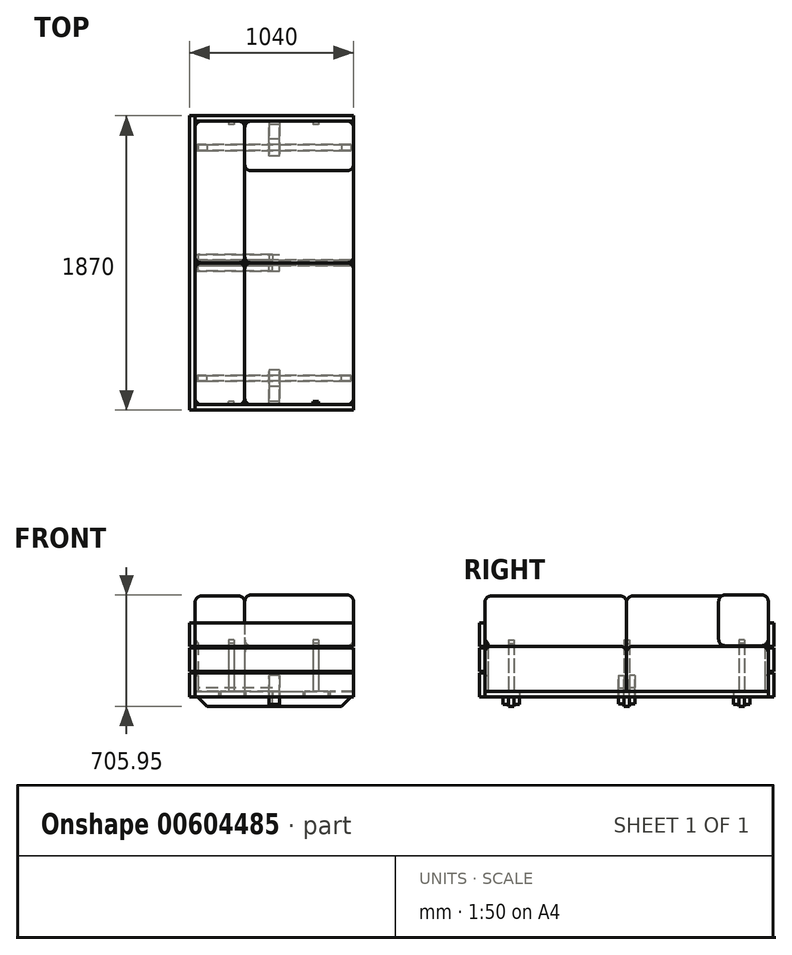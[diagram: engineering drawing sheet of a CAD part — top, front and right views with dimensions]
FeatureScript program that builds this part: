
annotation { "Feature Type Name" : "Feature", "Feature Type Description" : "" }
export const myFeature = defineFeature(function(context is Context, id is Id, definition is map)
    precondition{}
    {
        {
            var Q0;
            Q0=qCreatedBy(makeId("Front.planeOp"),FACE);
            var sketch = newSketch(context, id + "F0", { "sketchPlane" : qUnion([Q0])});
            skLineSegment(sketch, "E0.bottom", {"start": v(35, 530) * mm, "end": v(1040, 530) * mm});
            skLineSegment(sketch, "E0.top", {"start": v(35, 380) * mm, "end": v(1040, 380) * mm});
            skLineSegment(sketch, "E0.right", {"start": v(1040, 530) * mm, "end": v(1040, 380) * mm});
            skLineSegment(sketch, "E1.bottom", {"start": v(35, 370) * mm, "end": v(1040, 370) * mm});
            skLineSegment(sketch, "E1.top", {"start": v(35, 220) * mm, "end": v(1040, 220) * mm});
            skLineSegment(sketch, "E1.left", {"start": v(35, 370) * mm, "end": v(35, 220) * mm});
            skLineSegment(sketch, "E1.right", {"start": v(1040, 370) * mm, "end": v(1040, 220) * mm});
            skLineSegment(sketch, "E2.bottom", {"start": v(35, 210) * mm, "end": v(1040, 210) * mm});
            skLineSegment(sketch, "E2.top", {"start": v(35, 60) * mm, "end": v(1040, 60) * mm});
            skLineSegment(sketch, "E2.left", {"start": v(35, 210) * mm, "end": v(35, 60) * mm});
            skLineSegment(sketch, "E2.right", {"start": v(1040, 210) * mm, "end": v(1040, 60) * mm});
            skLineSegment(sketch, "E3", {"start": v(35, 380) * mm, "end": v(35, 530) * mm});
            skSolve(sketch);
        }
        {
            var Q0;
            Q0=qSketchRegion(id+"F0",true);
            extrude(context, id + "F1", {"entities" : qUnion([Q0]), "depth" : 935 * mm, "hasSecondDirection" : true, "secondDirectionOppositeDirection" : false, "secondDirectionDepth" : 900 * mm});
        }
        {
            var Q0;
            Q0=qSketchRegion(id+"F0",true);
            extrude(context, id + "F2", {"entities" : qUnion([Q0]), "oppositeDirection" : true, "depth" : 935 * mm, "hasSecondDirection" : true, "secondDirectionOppositeDirection" : true, "secondDirectionDepth" : 900 * mm});
        }
        {
            var Q0;
            Q0=qCreatedBy(makeId("Top.planeOp"),FACE);
            var sketch = newSketch(context, id + "F3", { "sketchPlane" : qUnion([Q0])});
            skLineSegment(sketch, "E4.bottom", {"start": v(1040, -900) * mm, "end": v(890, -900) * mm});
            skLineSegment(sketch, "E4.top", {"start": v(1040, 900) * mm, "end": v(890, 900) * mm});
            skLineSegment(sketch, "E4.left", {"start": v(1040, -900) * mm, "end": v(1040, 900) * mm});
            skLineSegment(sketch, "E4.right", {"start": v(890, -900) * mm, "end": v(890, 900) * mm});
            skLineSegment(sketch, "E5.bottom", {"start": v(880, -900) * mm, "end": v(730, -900) * mm});
            skLineSegment(sketch, "E5.top", {"start": v(880, 900) * mm, "end": v(730, 900) * mm});
            skLineSegment(sketch, "E5.left", {"start": v(880, -900) * mm, "end": v(880, 900) * mm});
            skLineSegment(sketch, "E5.right", {"start": v(730, -900) * mm, "end": v(730, 900) * mm});
            skLineSegment(sketch, "E6.bottom", {"start": v(505, -900) * mm, "end": v(355, -900) * mm});
            skLineSegment(sketch, "E6.top", {"start": v(505, 900) * mm, "end": v(355, 900) * mm});
            skLineSegment(sketch, "E6.left", {"start": v(505, -900) * mm, "end": v(505, 900) * mm});
            skLineSegment(sketch, "E6.right", {"start": v(355, -900) * mm, "end": v(355, 900) * mm});
            skLineSegment(sketch, "E7.bottom", {"start": v(345, -900) * mm, "end": v(195, -900) * mm});
            skLineSegment(sketch, "E7.top", {"start": v(345, 900) * mm, "end": v(195, 900) * mm});
            skLineSegment(sketch, "E7.left", {"start": v(345, -900) * mm, "end": v(345, 900) * mm});
            skLineSegment(sketch, "E7.right", {"start": v(195, -900) * mm, "end": v(195, 900) * mm});
            skLineSegment(sketch, "E8.bottom", {"start": v(185, -900) * mm, "end": v(35, -900) * mm});
            skLineSegment(sketch, "E8.top", {"start": v(185, 900) * mm, "end": v(35, 900) * mm});
            skLineSegment(sketch, "E8.left", {"start": v(185, -900) * mm, "end": v(185, 900) * mm});
            skLineSegment(sketch, "E8.right", {"start": v(35, 900) * mm, "end": v(35, -900) * mm});
            skLineSegment(sketch, "E9.bottom", {"start": v(570, 900) * mm, "end": v(720, 900) * mm});
            skLineSegment(sketch, "E9.top", {"start": v(570, -900) * mm, "end": v(720, -900) * mm});
            skLineSegment(sketch, "E9.left", {"start": v(570, 900) * mm, "end": v(570, -900) * mm});
            skLineSegment(sketch, "E9.right", {"start": v(720, 900) * mm, "end": v(720, -900) * mm});
            skSolve(sketch);
        }
        {
            var Q0;
            Q0=qSketchRegion(id+"F3",true);
            extrude(context, id + "F4", {"entities" : qUnion([Q0]), "depth" : 95 * mm, "hasSecondDirection" : true, "secondDirectionOppositeDirection" : false, "secondDirectionDepth" : 60 * mm});
        }
        {
            var Q0;
            Q0=qCreatedBy(makeId("Right.planeOp"),FACE);
            var sketch = newSketch(context, id + "F5", { "sketchPlane" : qUnion([Q0])});
            skLineSegment(sketch, "E10.bottom", {"start": v(935, 530) * mm, "end": v(-935, 530) * mm});
            skLineSegment(sketch, "E10.top", {"start": v(935, 380) * mm, "end": v(-935, 380) * mm});
            skLineSegment(sketch, "E10.left", {"start": v(935, 530) * mm, "end": v(935, 380) * mm});
            skLineSegment(sketch, "E10.right", {"start": v(-935, 530) * mm, "end": v(-935, 380) * mm});
            skLineSegment(sketch, "E11.bottom", {"start": v(935, 370) * mm, "end": v(-935, 370) * mm});
            skLineSegment(sketch, "E11.top", {"start": v(935, 220) * mm, "end": v(-935, 220) * mm});
            skLineSegment(sketch, "E11.left", {"start": v(935, 370) * mm, "end": v(935, 220) * mm});
            skLineSegment(sketch, "E11.right", {"start": v(-935, 370) * mm, "end": v(-935, 220) * mm});
            skLineSegment(sketch, "E12.bottom", {"start": v(935, 210) * mm, "end": v(-935, 210) * mm});
            skLineSegment(sketch, "E12.top", {"start": v(935, 60) * mm, "end": v(-935, 60) * mm});
            skLineSegment(sketch, "E12.left", {"start": v(935, 210) * mm, "end": v(935, 60) * mm});
            skLineSegment(sketch, "E12.right", {"start": v(-935, 210) * mm, "end": v(-935, 60) * mm});
            skSolve(sketch);
        }
        {
            var Q0;
            Q0=qSketchRegion(id+"F5",true);
            extrude(context, id + "F6", {"entities" : qUnion([Q0]), "depth" : 35 * mm});
        }
        {
            var Q0;
            Q0=qCreatedBy(makeId("Front.planeOp"),FACE);
            var sketch = newSketch(context, id + "F7", { "sketchPlane" : qUnion([Q0])});
            skLineSegment(sketch, "E13", {"start": v(50, 60) * mm, "end": v(110, 0) * mm});
            skLineSegment(sketch, "E14", {"start": v(110, 0) * mm, "end": v(965, 0) * mm});
            skLineSegment(sketch, "E15", {"start": v(965, 0) * mm, "end": v(1025, 60) * mm});
            skLineSegment(sketch, "E16", {"start": v(1025, 60) * mm, "end": v(50, 60) * mm});
            skSolve(sketch);
        }
        {
            var Q0;
            Q0=makeQuery(id+"F7.imprint","IMPRINT",FACE,{"disambiguationData":[TD([[makeQuery(id+"F7.imprint","IMPRINT",EDGE,{"derivedFrom":sQuery(id+"F7.wireOp",EDGE,"E13")}),1.0]])]});
            extrude(context, id + "F8", {"entities" : qUnion([Q0]), "depth" : 17.5 * mm, "hasSecondDirection" : true, "secondDirectionOppositeDirection" : true, "secondDirectionDepth" : 17.5 * mm});
        }
        {
            var Q0;
            Q0=qSketchRegion(id+"F7",true);
            extrude(context, id + "F9", {"entities" : qUnion([Q0]), "depth" : 750 * mm, "hasSecondDirection" : true, "secondDirectionOppositeDirection" : false, "secondDirectionDepth" : 715 * mm});
        }
        {
            var Q0;
            Q0=qSketchRegion(id+"F7",true);
            extrude(context, id + "F10", {"entities" : qUnion([Q0]), "oppositeDirection" : true, "depth" : 750 * mm, "hasSecondDirection" : true, "secondDirectionOppositeDirection" : true, "secondDirectionDepth" : 715 * mm});
        }
        {
            var Q0;
            Q0=qCreatedBy(makeId("Front.planeOp"),FACE);
            var sketch = newSketch(context, id + "F11", { "sketchPlane" : qUnion([Q0])});
            skLineSegment(sketch, "E17.top", {"start": v(35, 95) * mm, "end": v(55, 95) * mm});
            skLineSegment(sketch, "E17.left", {"start": v(35, 420) * mm, "end": v(35, 95) * mm});
            skLineSegment(sketch, "E17.right", {"start": v(55, 400) * mm, "end": v(55, 95) * mm});
            skLineSegment(sketch, "E18", {"start": v(35, 420) * mm, "end": v(55, 400) * mm});
            skSolve(sketch);
        }
        {
            var Q0;
            Q0=qSketchRegion(id+"F11",true);
            extrude(context, id + "F12", {"entities" : qUnion([Q0]), "depth" : 17.5 * mm, "hasSecondDirection" : true, "secondDirectionOppositeDirection" : true, "secondDirectionDepth" : 17.5 * mm});
        }
        {
            var Q0;
            Q0=qSketchRegion(id+"F11",true);
            extrude(context, id + "F13", {"entities" : qUnion([Q0]), "depth" : 750 * mm, "hasSecondDirection" : true, "secondDirectionOppositeDirection" : false, "secondDirectionDepth" : 715 * mm});
        }
        {
            var Q0;
            Q0=qSketchRegion(id+"F11",true);
            extrude(context, id + "F14", {"entities" : qUnion([Q0]), "oppositeDirection" : true, "depth" : 750 * mm, "hasSecondDirection" : true, "secondDirectionOppositeDirection" : true, "secondDirectionDepth" : 715 * mm});
        }
        {
            var Q0;
            Q0=qCreatedBy(makeId("Front.planeOp"),FACE);
            var sketch = newSketch(context, id + "F15", { "sketchPlane" : qUnion([Q0])});
            skLineSegment(sketch, "E19.bottom", {"start": v(35, 195) * mm, "end": v(55, 195) * mm});
            skLineSegment(sketch, "E19.top", {"start": v(35, 95) * mm, "end": v(55, 95) * mm});
            skLineSegment(sketch, "E19.left", {"start": v(35, 95) * mm, "end": v(35, 195) * mm});
            skLineSegment(sketch, "E19.right", {"start": v(55, 145) * mm, "end": v(55, 195) * mm});
            skLineSegment(sketch, "E20.top", {"start": v(55, 95) * mm, "end": v(505, 95) * mm});
            skLineSegment(sketch, "E20.left", {"start": v(55, 145) * mm, "end": v(55, 115) * mm});
            skLineSegment(sketch, "E20.right", {"start": v(525, 115) * mm, "end": v(525, 95) * mm});
            skLineSegment(sketch, "E21.top", {"start": v(505, 15) * mm, "end": v(525, 15) * mm});
            skLineSegment(sketch, "E21.left", {"start": v(505, 95) * mm, "end": v(505, 15) * mm});
            skLineSegment(sketch, "E22", {"start": v(525, 115) * mm, "end": v(55, 115) * mm});
            skLineSegment(sketch, "E23", {"start": v(525, 15) * mm, "end": v(525, 95) * mm});
            skSolve(sketch);
        }
        {
            var Q0;
            Q0=qSketchRegion(id+"F15",true);
            extrude(context, id + "F16", {"entities" : qUnion([Q0]), "depth" : 52.5 * mm, "hasSecondDirection" : true, "secondDirectionOppositeDirection" : false, "secondDirectionDepth" : 17.5 * mm});
        }
        {
            var Q0;
            Q0=qSketchRegion(id+"F15",true);
            extrude(context, id + "F17", {"entities" : qUnion([Q0]), "oppositeDirection" : true, "depth" : 52.5 * mm, "hasSecondDirection" : true, "secondDirectionOppositeDirection" : true, "secondDirectionDepth" : 17.5 * mm});
        }
        {
            var Q0;
            Q0=qCreatedBy(makeId("Front.planeOp"),FACE);
            var sketch = newSketch(context, id + "F18", { "sketchPlane" : qUnion([Q0])});
            skLineSegment(sketch, "E24.bottom", {"start": v(525, 95) * mm, "end": v(570, 95) * mm});
            skLineSegment(sketch, "E24.top", {"start": v(525, 60) * mm, "end": v(570, 60) * mm});
            skLineSegment(sketch, "E24.left", {"start": v(525, 95) * mm, "end": v(525, 60) * mm});
            skLineSegment(sketch, "E24.right", {"start": v(570, 95) * mm, "end": v(570, 60) * mm});
            skSolve(sketch);
        }
        {
            var Q0;
            Q0=makeQuery(id+"F18.imprint","IMPRINT",FACE,{"disambiguationData":[TD([[makeQuery(id+"F18.imprint","IMPRINT",EDGE,{"derivedFrom":sQuery(id+"F18.wireOp",EDGE,"E24.bottom")}),-1.0]])]});
            extrude(context, id + "F19", {"entities" : qUnion([Q0]), "depth" : 52.5 * mm, "hasSecondDirection" : true, "secondDirectionOppositeDirection" : true, "secondDirectionDepth" : 52.5 * mm});
        }
        {
            var Q0;
            Q0=qCreatedBy(makeId("Right.planeOp"),FACE);
            var sketch = newSketch(context, id + "F20", { "sketchPlane" : qUnion([Q0])});
            skLineSegment(sketch, "E25.top", {"start": v(-900, 95) * mm, "end": v(-880, 95) * mm});
            skLineSegment(sketch, "E25.left", {"start": v(-900, 420) * mm, "end": v(-900, 95) * mm});
            skLineSegment(sketch, "E25.right", {"start": v(-880, 400) * mm, "end": v(-880, 95) * mm});
            skLineSegment(sketch, "E26", {"start": v(-900, 420) * mm, "end": v(-880, 400) * mm});
            skSolve(sketch);
        }
        {
            var Q0;
            Q0=qSketchRegion(id+"F20",true);
            extrude(context, id + "F21", {"entities" : qUnion([Q0]), "depth" : 282.5 * mm, "hasSecondDirection" : true, "secondDirectionOppositeDirection" : false, "secondDirectionDepth" : 247.5 * mm});
        }
        {
            var Q0;
            Q0=qSketchRegion(id+"F20",true);
            extrude(context, id + "F22", {"entities" : qUnion([Q0]), "depth" : 817.5 * mm, "hasSecondDirection" : true, "secondDirectionOppositeDirection" : false, "secondDirectionDepth" : 782.5 * mm});
        }
        {
            var Q0;
            Q0=qCreatedBy(makeId("Right.planeOp"),FACE);
            var sketch = newSketch(context, id + "F23", { "sketchPlane" : qUnion([Q0])});
            skLineSegment(sketch, "E27", {"start": v(-900, 60) * mm, "end": v(-900, 195) * mm});
            skLineSegment(sketch, "E28", {"start": v(-900, 195) * mm, "end": v(-880, 195) * mm});
            skLineSegment(sketch, "E29", {"start": v(-880, 195) * mm, "end": v(-880, 95) * mm});
            skLineSegment(sketch, "E30", {"start": v(-880, 95) * mm, "end": v(-680, 95) * mm});
            skLineSegment(sketch, "E31", {"start": v(-680, 95) * mm, "end": v(-680, 10) * mm});
            skLineSegment(sketch, "E32", {"start": v(-680, 10) * mm, "end": v(-715, 10) * mm});
            skLineSegment(sketch, "E33", {"start": v(-715, 10) * mm, "end": v(-715, 60) * mm});
            skLineSegment(sketch, "E34", {"start": v(-715, 60) * mm, "end": v(-750, 60) * mm});
            skLineSegment(sketch, "E35", {"start": v(-750, 60) * mm, "end": v(-750, 10) * mm});
            skLineSegment(sketch, "E36", {"start": v(-750, 10) * mm, "end": v(-785, 10) * mm});
            skLineSegment(sketch, "E37", {"start": v(-785, 10) * mm, "end": v(-785, 60) * mm});
            skLineSegment(sketch, "E38", {"start": v(-785, 60) * mm, "end": v(-900, 60) * mm});
            skSolve(sketch);
        }
        {
            var Q0;
            Q0=qSketchRegion(id+"F23",true);
            extrude(context, id + "F24", {"entities" : qUnion([Q0]), "depth" : 570 * mm, "hasSecondDirection" : true, "secondDirectionOppositeDirection" : false, "secondDirectionDepth" : 505 * mm});
        }
        {
            var Q0;
            Q0=makeQuery(id+"F22.opExtrude","SWEPT_BODY",BODY,{"disambiguationData":[OSD([sQuery(id+"F20.wireOp",EDGE,"E25.top"),sQuery(id+"F20.wireOp",EDGE,"E25.left"),sQuery(id+"F20.wireOp",EDGE,"E25.right"),sQuery(id+"F20.wireOp",EDGE,"E26")])]});
            var Q1;
            Q1=qCreatedBy(makeId("Front.planeOp"),FACE);
            mirror(context, id + "F25", {"entities" : qUnion([Q0]), "mirrorPlane" : qUnion([Q1])});
        }
        {
            var Q0;
            Q0=makeQuery(id+"F21.opExtrude","SWEPT_BODY",BODY,{"disambiguationData":[OSD([sQuery(id+"F20.wireOp",EDGE,"E25.top"),sQuery(id+"F20.wireOp",EDGE,"E25.left"),sQuery(id+"F20.wireOp",EDGE,"E25.right"),sQuery(id+"F20.wireOp",EDGE,"E26")])]});
            var Q1;
            Q1=qCreatedBy(makeId("Front.planeOp"),FACE);
            mirror(context, id + "F26", {"entities" : qUnion([Q0]), "mirrorPlane" : qUnion([Q1])});
        }
        {
            var Q0;
            Q0=makeQuery(id+"F24.opExtrude","SWEPT_BODY",BODY,{"disambiguationData":[OSD([sQuery(id+"F23.wireOp",EDGE,"E27"),sQuery(id+"F23.wireOp",EDGE,"E28"),sQuery(id+"F23.wireOp",EDGE,"E29"),sQuery(id+"F23.wireOp",EDGE,"E30"),sQuery(id+"F23.wireOp",EDGE,"E31"),sQuery(id+"F23.wireOp",EDGE,"E32"),sQuery(id+"F23.wireOp",EDGE,"E33"),sQuery(id+"F23.wireOp",EDGE,"E34"),sQuery(id+"F23.wireOp",EDGE,"E35"),sQuery(id+"F23.wireOp",EDGE,"E36"),sQuery(id+"F23.wireOp",EDGE,"E37"),sQuery(id+"F23.wireOp",EDGE,"E38")])]});
            var Q1;
            Q1=qCreatedBy(makeId("Front.planeOp"),FACE);
            mirror(context, id + "F27", {"entities" : qUnion([Q0]), "mirrorPlane" : qUnion([Q1])});
        }
        {
            var Q0;
            Q0=qCreatedBy(makeId("Front.planeOp"),FACE);
            var sketch = newSketch(context, id + "F28", { "sketchPlane" : qUnion([Q0])});
            skLineSegment(sketch, "E39.bottom", {"start": v(390, 380) * mm, "end": v(1000, 380) * mm});
            skLineSegment(sketch, "E39.top", {"start": v(350, 95) * mm, "end": v(1040, 95) * mm});
            skLineSegment(sketch, "E39.left", {"start": v(350, 340) * mm, "end": v(350, 95) * mm});
            skLineSegment(sketch, "E39.right", {"start": v(1040, 340) * mm, "end": v(1040, 95) * mm});
            skPoint(sketch, "E40.visualSharp", {"position": v(1040, 380) * mm});
            skArc(sketch, "E40.filletArc", {"start": v(1040, 340) * mm, "mid": v(1028.28, 368.28) * mm, "end": v(1000, 380) * mm});
            skPoint(sketch, "E41.visualSharp", {"position": v(350, 380) * mm});
            skArc(sketch, "E41.filletArc", {"start": v(390, 380) * mm, "mid": v(361.72, 368.28) * mm, "end": v(350, 340) * mm});
            skSolve(sketch);
        }
        {
            var Q0;
            Q0=qSketchRegion(id+"F28",true);
            extrude(context, id + "F29", {"entities" : qUnion([Q0]), "depth" : 900 * mm});
        }
        {
            var Q0;
            Q0=makeQuery(id+"F29.opExtrude","CAP_EDGE",EDGE,{"disambiguationData":[OSD([sQuery(id+"F28.wireOp",EDGE,"E39.bottom")])],"isStart":true});
            fillet(context, id + "F30", {"entities" : qUnion([Q0]), "radius" : 40 * mm, "tangentPropagation" : true, "allowEdgeOverflow" : false});
        }
        {
            var Q0;
            Q0=makeQuery(id+"F29.opExtrude","CAP_EDGE",EDGE,{"disambiguationData":[OSD([sQuery(id+"F28.wireOp",EDGE,"E39.bottom")])],"isStart":false});
            fillet(context, id + "F31", {"entities" : qUnion([Q0]), "radius" : 40 * mm, "tangentPropagation" : true, "allowEdgeOverflow" : false});
        }
        {
            var Q0;
            Q0=makeQuery(id+"F29.opExtrude","SWEPT_BODY",BODY,{"disambiguationData":[OSD([sQuery(id+"F28.wireOp",EDGE,"E39.bottom"),sQuery(id+"F28.wireOp",EDGE,"E39.top"),sQuery(id+"F28.wireOp",EDGE,"E39.left"),sQuery(id+"F28.wireOp",EDGE,"E39.right"),sQuery(id+"F28.wireOp",EDGE,"E40.filletArc")])]});
            var Q1;
            Q1=qCreatedBy(makeId("Front.planeOp"),FACE);
            mirror(context, id + "F32", {"entities" : qUnion([Q0]), "mirrorPlane" : qUnion([Q1])});
        }
        {
            var Q0;
            Q0=qCreatedBy(makeId("Front.planeOp"),FACE);
            var sketch = newSketch(context, id + "F33", { "sketchPlane" : qUnion([Q0])});
            skLineSegment(sketch, "E42.bottom", {"start": v(75, 700) * mm, "end": v(310, 700) * mm});
            skLineSegment(sketch, "E42.top", {"start": v(35, 95) * mm, "end": v(350, 95) * mm});
            skLineSegment(sketch, "E42.left", {"start": v(35, 660) * mm, "end": v(35, 95) * mm});
            skLineSegment(sketch, "E42.right", {"start": v(350, 660) * mm, "end": v(350, 95) * mm});
            skPoint(sketch, "E43.visualSharp", {"position": v(35, 700) * mm});
            skArc(sketch, "E43.filletArc", {"start": v(75, 700) * mm, "mid": v(46.72, 688.28) * mm, "end": v(35, 660) * mm});
            skPoint(sketch, "E44.visualSharp", {"position": v(350, 700) * mm});
            skArc(sketch, "E44.filletArc", {"start": v(350, 660) * mm, "mid": v(338.28, 688.28) * mm, "end": v(310, 700) * mm});
            skSolve(sketch);
        }
        {
            var Q0;
            Q0=qSketchRegion(id+"F33",true);
            extrude(context, id + "F34", {"entities" : qUnion([Q0]), "depth" : 900 * mm});
        }
        {
            var Q0;
            Q0=makeQuery(id+"F34.opExtrude","CAP_EDGE",EDGE,{"disambiguationData":[OSD([sQuery(id+"F33.wireOp",EDGE,"E42.right")])],"isStart":true});
            var Q1;
            Q1=makeQuery(id+"F34.opExtrude","CAP_EDGE",EDGE,{"disambiguationData":[OSD([sQuery(id+"F33.wireOp",EDGE,"E42.bottom")])],"isStart":false});
            fillet(context, id + "F35", {"entities" : qUnion([Q0, Q1]), "radius" : 40 * mm, "tangentPropagation" : true, "allowEdgeOverflow" : false});
        }
        {
            var Q0;
            Q0=makeQuery(id+"F34.opExtrude","SWEPT_BODY",BODY,{"disambiguationData":[OSD([sQuery(id+"F33.wireOp",EDGE,"E42.bottom"),sQuery(id+"F33.wireOp",EDGE,"E42.top"),sQuery(id+"F33.wireOp",EDGE,"E42.left"),sQuery(id+"F33.wireOp",EDGE,"E42.right"),sQuery(id+"F33.wireOp",EDGE,"E43.filletArc"),sQuery(id+"F33.wireOp",EDGE,"E44.filletArc")])]});
            var Q1;
            Q1=qCreatedBy(makeId("Front.planeOp"),FACE);
            mirror(context, id + "F36", {"entities" : qUnion([Q0]), "mirrorPlane" : qUnion([Q1])});
        }
        {
            var Q0;
            Q0=qCreatedBy(makeId("Right.planeOp"),FACE);
            var sketch = newSketch(context, id + "F37", { "sketchPlane" : qUnion([Q0])});
            skLineSegment(sketch, "E45.bottom", {"start": v(625, 705.95) * mm, "end": v(860, 705.95) * mm});
            skLineSegment(sketch, "E45.top", {"start": v(625, 384.52) * mm, "end": v(860, 384.52) * mm});
            skLineSegment(sketch, "E45.left", {"start": v(585, 665.95) * mm, "end": v(585, 424.52) * mm});
            skLineSegment(sketch, "E45.right", {"start": v(900, 665.95) * mm, "end": v(900, 424.52) * mm});
            skPoint(sketch, "E46.visualSharp", {"position": v(585, 705.95) * mm});
            skArc(sketch, "E46.filletArc", {"start": v(625, 705.95) * mm, "mid": v(596.72, 694.23) * mm, "end": v(585, 665.95) * mm});
            skPoint(sketch, "E47.visualSharp", {"position": v(900, 705.95) * mm});
            skArc(sketch, "E47.filletArc", {"start": v(900, 665.95) * mm, "mid": v(888.28, 694.23) * mm, "end": v(860, 705.95) * mm});
            skPoint(sketch, "E48.visualSharp", {"position": v(585, 384.52) * mm});
            skArc(sketch, "E48.filletArc", {"start": v(585, 424.52) * mm, "mid": v(596.72, 396.23) * mm, "end": v(625, 384.52) * mm});
            skPoint(sketch, "E49.visualSharp", {"position": v(900, 384.52) * mm});
            skArc(sketch, "E49.filletArc", {"start": v(860, 384.52) * mm, "mid": v(888.28, 396.23) * mm, "end": v(900, 424.52) * mm});
            skSolve(sketch);
        }
        {
            var Q0;
            Q0=makeQuery(id+"F37.imprint","IMPRINT",FACE,{"disambiguationData":[TD([[makeQuery(id+"F37.imprint","IMPRINT",EDGE,{"derivedFrom":sQuery(id+"F37.wireOp",EDGE,"E45.bottom")}),-1.0]])]});
            extrude(context, id + "F38", {"entities" : qUnion([Q0]), "depth" : 1040 * mm, "hasSecondDirection" : true, "secondDirectionOppositeDirection" : false, "secondDirectionDepth" : 350 * mm});
        }
        {
            var Q0;
            Q0=makeQuery(id+"F38.opExtrude","CAP_EDGE",EDGE,{"disambiguationData":[OSD([sQuery(id+"F37.wireOp",EDGE,"E45.left")])],"isStart":false});
            fillet(context, id + "F39", {"entities" : qUnion([Q0]), "radius" : 40 * mm, "tangentPropagation" : true, "allowEdgeOverflow" : false});
        }
        {
            var Q0;
            Q0=makeQuery(id+"F38.opExtrude","CAP_EDGE",EDGE,{"disambiguationData":[OSD([sQuery(id+"F37.wireOp",EDGE,"E46.filletArc")])],"isStart":true});
            fillet(context, id + "F40", {"entities" : qUnion([Q0]), "radius" : 40 * mm, "tangentPropagation" : true, "allowEdgeOverflow" : false});
        }
    });
